# Revit family: Shower-Showerhead-KOHLER-Loure-K-45215
name_source: partatom
category: Plumbing Fixtures
revit_build: Autodesk Revit 2015 (Build: 20140606_1530(x64)
units: mm (PartAtom-declared; Revit-internal decimal feet)

## types (6) — shared parameters
ADA Compliant = No
Assembly Code = D2010700
CW Connection = No
Cold Water Inlet = Cold Water Inlet
Date Modified = 09/10/2018
Default Elevation = 0"
Flow Rate = 2 GPM
HW Connection = Yes
Height = 3 7/8"
Hot Water Inlet = Hot Water Inlet
Length = 5 1/4"
Manufacturer = KOHLER Co.
MasterFormat 1995 = 15410
MasterFormat 2004 = 22.41.23
Material = Premium Metal Construction
Panel Thickness = 0"
Pressure = 80.00 psi
Product Documentation Link = http://www.us.kohler.com
Product Name = Loure
Product Page URL = http://www.us.kohler.com
Tempered Water Inlet = Tempered Water Inlet
URL = https://www.us.kohler.com
Vent Connection = No
Waste Connection = No
Waste Water Outlet = Waste Water Outlet
Width = 6 5/16"

## per-type parameters (varying)
| type | Description | Finish | Model | Type |
| 2 GPM, CP-Polished Chrome | 2.0 gpm single-function showerhead with Katalyst air-induction technology | Kohler-Metal-CP-Polished_Chrome | K-45215-CP | 1 |
| 2 GPM, SN-Vibrant Polished Nickel | 2.0 gpm single-function showerhead with Katalyst air-induction technology | Kohler-Metal-SN-Vibrant_Polished_Nickel | K-45215-SN | 2 |
| 2 GPM, BN-Vibrant Brushed Nickel | 2.0 gpm single-function showerhead with Katalyst air-induction technology | Kohler-Metal-BN-Vibrant_Brushed_Nickel | K-45215-BN | 3 |
| 1.75 GPM, BN-Vibrant Brushed Nickel | 1.75 gpm single-function showerhead with Katalyst air-induction technology | Kohler-Metal-BN-Vibrant_Brushed_Nickel | K-45215-G-BN | 6 |
| 1.75 GPM, SN-Vibrant Polished Nickel | 1.75 gpm single-function showerhead with Katalyst air-induction technology | Kohler-Metal-SN-Vibrant_Polished_Nickel | K-45215-G-SN | 5 |
| 1.75 GPM, CP-Polished Chrome | 1.75 gpm single-function showerhead with Katalyst air-induction technology | Kohler-Metal-CP-Polished_Chrome | K-45215-G-CP | 4 |

## geometry (parser evidence)
native form markers: Sweep x6
no freeform markers — native parametric forms only
